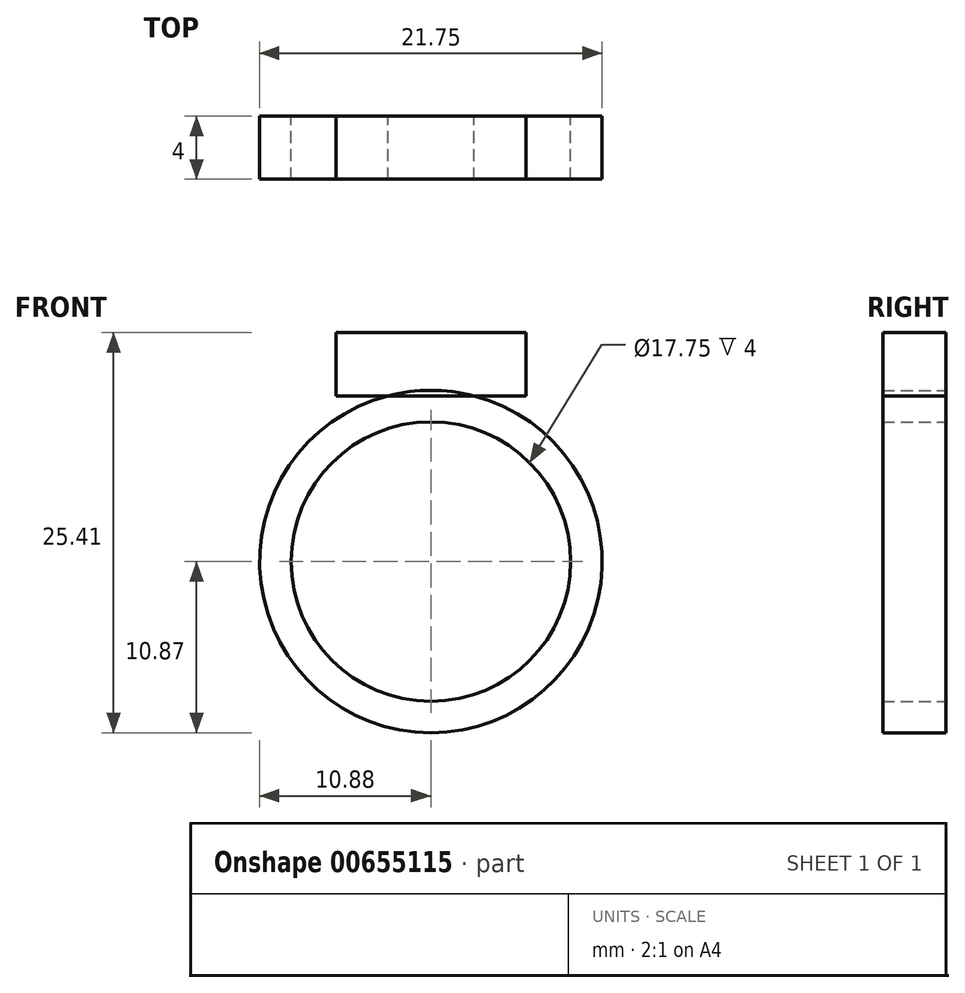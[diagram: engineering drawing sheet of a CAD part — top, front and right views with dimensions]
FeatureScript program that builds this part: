
annotation { "Feature Type Name" : "Feature", "Feature Type Description" : "" }
export const myFeature = defineFeature(function(context is Context, id is Id, definition is map)
    precondition{}
    {
        {
            var Q0;
            Q0=qCreatedBy(makeId("Front.planeOp"),FACE);
            var sketch = newSketch(context, id + "F0", { "sketchPlane" : qUnion([Q0])});
            skCircle(sketch, "E0", {"center": v(0, 0) * mm, "radius": 8.88 * mm});
            skCircle(sketch, "E1.0", {"center": v(0, 0) * mm, "radius": 10.88 * mm});
            skLineSegment(sketch, "E2.bottom", {"start": v(6.03, 10.53) * mm, "end": v(-6.03, 10.53) * mm});
            skLineSegment(sketch, "E2.top", {"start": v(6.03, 14.54) * mm, "end": v(-6.03, 14.54) * mm});
            skLineSegment(sketch, "E2.left", {"start": v(6.03, 10.53) * mm, "end": v(6.03, 14.54) * mm});
            skLineSegment(sketch, "E2.right", {"start": v(-6.03, 10.53) * mm, "end": v(-6.03, 14.54) * mm});
            skPoint(sketch, "E2.middle", {"position": v(0, 12.53) * mm});
            skSolve(sketch);
        }
        {
            var Q0;
            Q0=makeQuery(id+"F0.imprint","IMPRINT",FACE,{"disambiguationData":[TD([[makeQuery(id+"F0.imprint","IMPRINT",EDGE,{"derivedFrom":sQuery(id+"F0.wireOp",EDGE,"E0")}),-1.0]])]});
            extrude(context, id + "F1", {"entities" : qUnion([Q0]), "depth" : 2 * mm, "offsetDistance" : 25 * mm, "hasSecondDirection" : true, "secondDirectionOppositeDirection" : true, "secondDirectionDepth" : 2 * mm});
        }
        {
            var Q0;
            Q0=makeQuery(id+"F1.opExtrude","CAP_EDGE",EDGE,{"disambiguationData":[OSD([sQuery(id+"F0.wireOp",EDGE,"E1.0")])],"isStart":false});
            var Q1;
            Q1=makeQuery(id+"F1.opExtrude","CAP_EDGE",EDGE,{"disambiguationData":[OSD([sQuery(id+"F0.wireOp",EDGE,"E0")])],"isStart":false});
            var Q2;
            Q2=makeQuery(id+"F1.opExtrude","CAP_EDGE",EDGE,{"disambiguationData":[OSD([sQuery(id+"F0.wireOp",EDGE,"E0")])],"isStart":true});
            var Q3;
            Q3=makeQuery(id+"F1.opExtrude","CAP_EDGE",EDGE,{"disambiguationData":[OSD([sQuery(id+"F0.wireOp",EDGE,"E1.0")])],"isStart":true});
            fillet(context, id + "F2", {"entities" : qUnion([Q0, Q1, Q2, Q3]), "radius" : 1 * mm, "tangentPropagation" : true, "allowEdgeOverflow" : false});
        }
        {
            var Q0;
            Q0=makeQuery(id+"F0.imprint","IMPRINT",FACE,{"disambiguationData":[TD([[makeQuery(id+"F0.imprint","IMPRINT",EDGE,{"derivedFrom":sQuery(id+"F0.wireOp",EDGE,"E2.top")}),1.0]])]});
            var Q1;
            {var subQ0=sQuery(id+"F0.wireOp",EDGE,"E2.bottom");var subQ1=sQuery(id+"F0.wireOp",EDGE,"E1.0");var subQ2=makeQuery(id+"F0.imprint","INTERSECT",VERTEX,{"disambiguationData":[OD(0.0)],"derivedFrom":[subQ1,subQ0]});Q1=makeQuery(id+"F0.imprint","IMPRINT",FACE,{"disambiguationData":[TD([[makeQuery(id+"F0.imprint","IMPRINT",EDGE,{"disambiguationData":[TD([[subQ2,-1.0]])],"derivedFrom":subQ1}),1.0]])]});}
            extrude(context, id + "F3", {"entities" : qUnion([Q0, Q1]), "operationType" : NewBodyOperationType.ADD, "depth" : 2 * mm, "offsetDistance" : 25 * mm, "hasSecondDirection" : true, "secondDirectionOppositeDirection" : true, "secondDirectionDepth" : 2 * mm});
        }
    });
